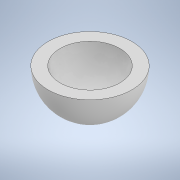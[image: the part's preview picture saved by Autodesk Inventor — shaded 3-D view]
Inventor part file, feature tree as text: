
AUTODESK INVENTOR PART (.ipt)
format: ipt  version: 2022 (Build 260153000, 153)  size: 318,976 bytes
history: native  units: in
note: dims shown in document units (in); Inventor stores cm internally (conversion verified against a paired STEP export)
features: revolve x1, shell x1, sketch x1
ambient origin geometry x8: Origin, YZ Plane, XZ Plane, XY Plane, X Axis, Y Axis, Z Axis, Center Point
bodies: Solid1 (feature_tree)
feature tree (3):
  revolve  "Revolution1"  [1 undecoded]
  shell  "Shell1"  [1 undecoded]
  sketch  "Sketch1"  dims[d3=90.0deg d4=0.3in]
note: 2 required parameter values undecoded (feature->parameter linkage not recoverable at this tier; creation-order binding heuristic only, values carry confidence <= 0.55)